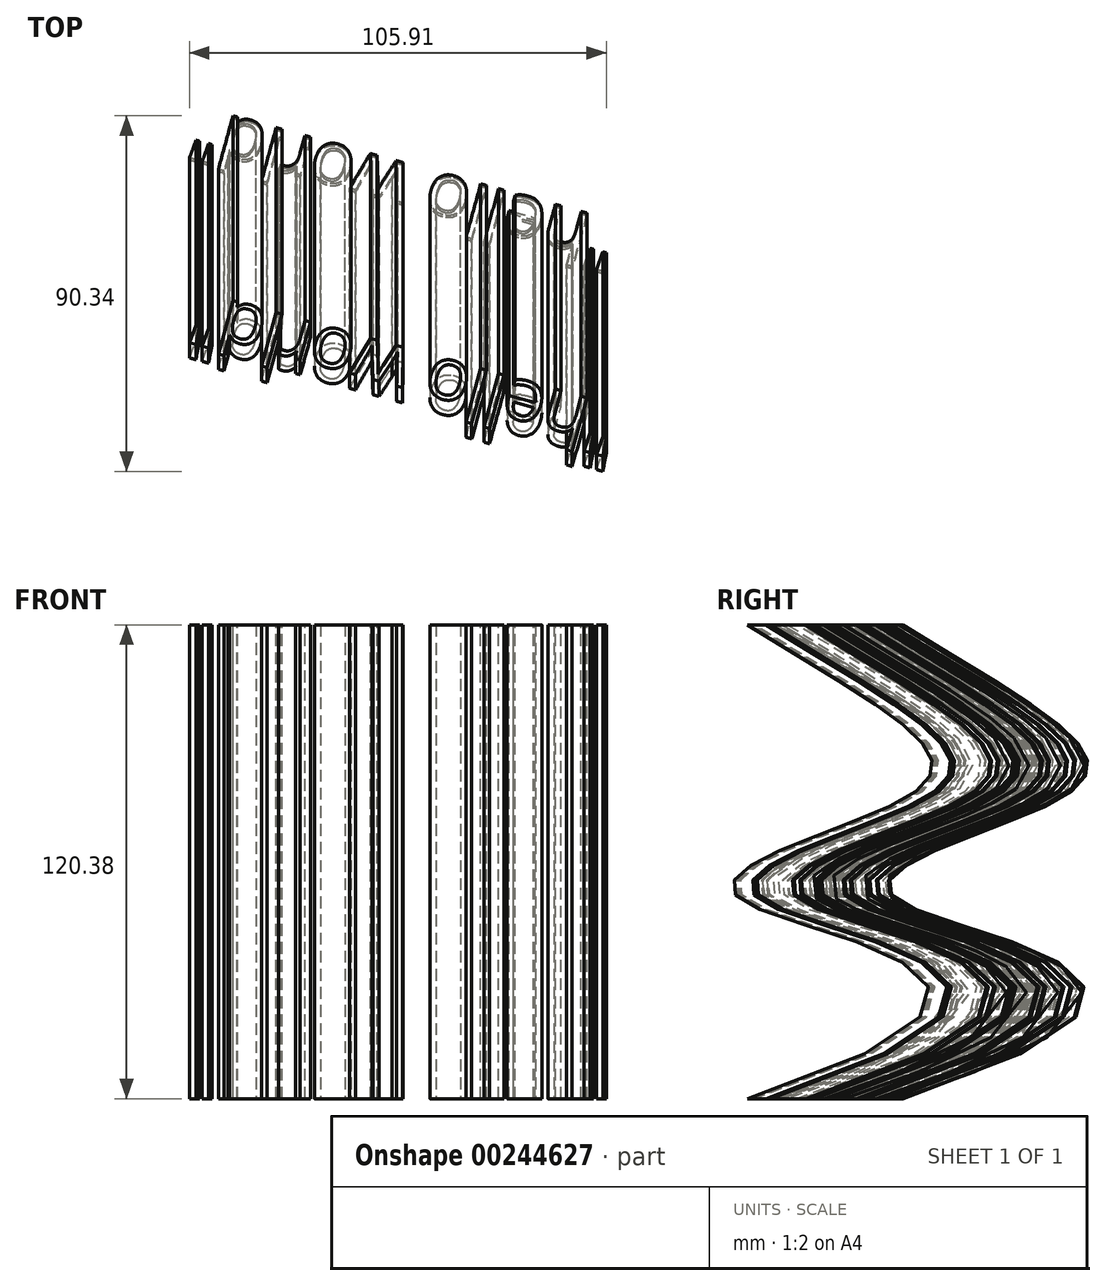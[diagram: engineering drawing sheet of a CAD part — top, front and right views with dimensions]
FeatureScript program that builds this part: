
annotation { "Feature Type Name" : "Feature", "Feature Type Description" : "" }
export const myFeature = defineFeature(function(context is Context, id is Id, definition is map)
    precondition{}
    {
        {
            var Q0;
            Q0=qCreatedBy(makeId("Top.planeOp"),FACE);
            cPlane(context, id + "F0", {"entities" : qUnion([Q0]), "cplaneType" : CPlaneType.OFFSET, "offset" : 127 * mm, "oppositeDirection" : true, "width" : 152.4 * mm, "height" : 152.4 * mm});
        }
        {
            var Q0;
            Q0=qCreatedBy(id+"F0.planeOp",FACE);
            var sketch = newSketch(context, id + "F1", { "sketchPlane" : qUnion([Q0])});
            skText(sketch, "E0", { "text": "\"hello world\"", "fontName": "OpenSans-Regular.ttf"});
            const initialGuessF1  = {"E0": [0.18404, -0.03853, -0.9643, 0.26478, 0.01335]};
            skSetInitialGuess(sketch, initialGuessF1);
            skSolve(sketch);
        }
        {
            var Q0;
            Q0=qCreatedBy(makeId("Right.planeOp"),FACE);
            var sketch = newSketch(context, id + "F2", { "sketchPlane" : qUnion([Q0])});
            skFitSpline(sketch, "E1", {"points": [v(0, 0) * mm, v(42.05, -42.8) * mm, v(0, -70.84) * mm, v(0, -120.38) * mm], "startDerivative": vector(300.14, -186.08) * mm, "endDerivative": vector(-888.7, -288.97) * mm});
            skSolve(sketch);
        }
        {
            var Q0;
            Q0 = qSketchRegion(id + "F1", true);
            var Q1;
            Q1=sQuery(id+"F2.wireOp",EDGE,"E1");
            sweep(context, id + "F3", {"profiles" : qUnion([Q0]), "path" : qUnion([Q1]), "keepProfileOrientation" : true});
        }
    });
